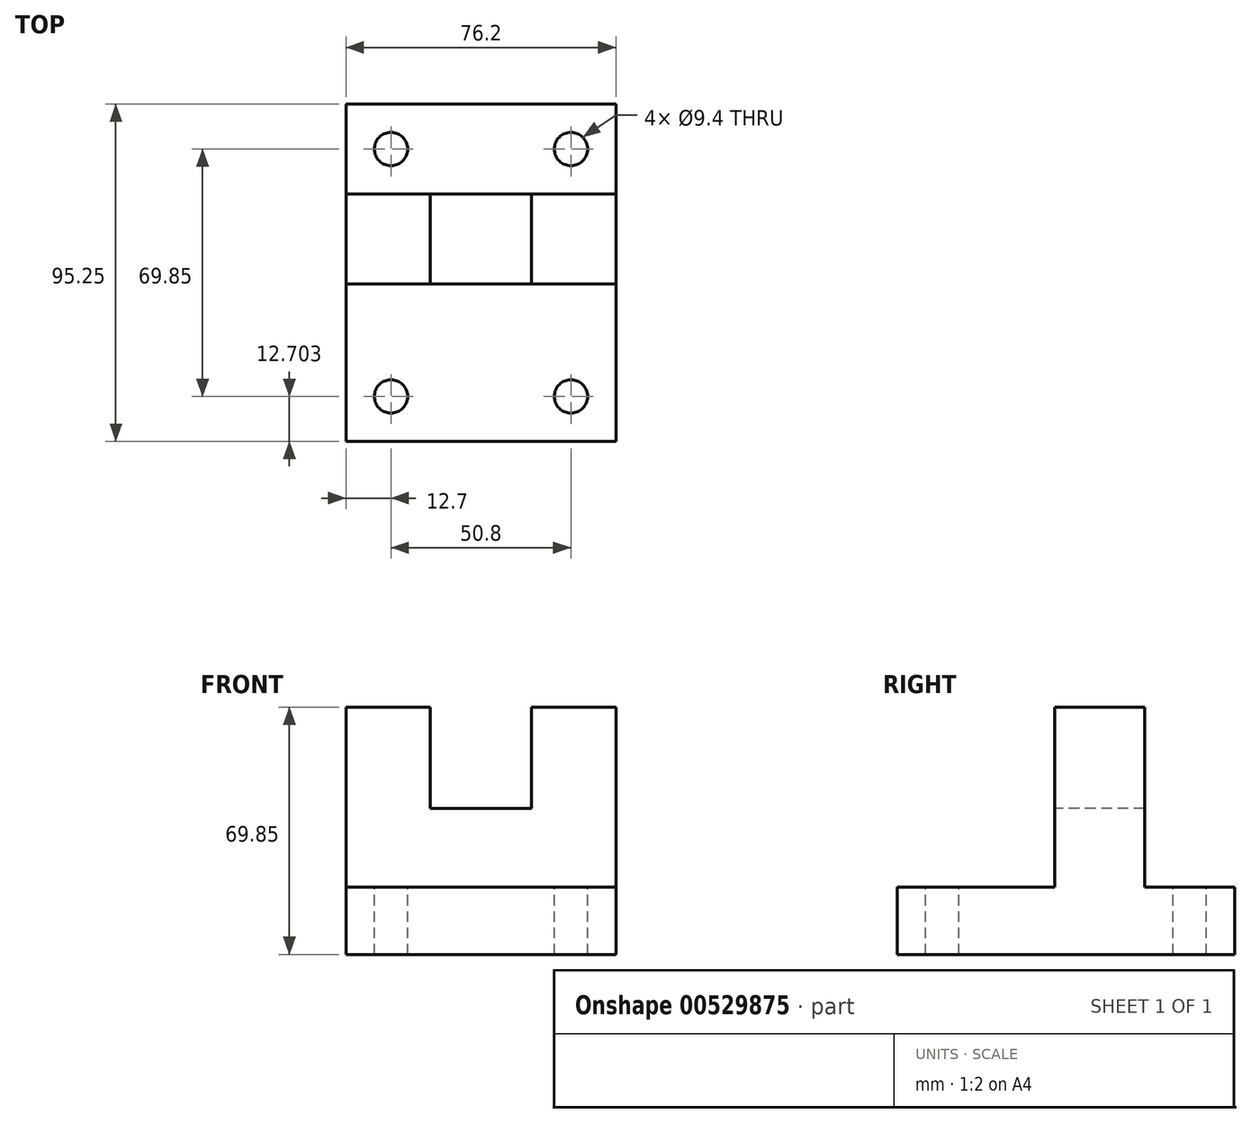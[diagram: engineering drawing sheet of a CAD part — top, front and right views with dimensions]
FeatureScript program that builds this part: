
annotation { "Feature Type Name" : "Feature", "Feature Type Description" : "" }
export const myFeature = defineFeature(function(context is Context, id is Id, definition is map)
    precondition{}
    {
        {
            var Q0;
            Q0=qCreatedBy(makeId("Right.planeOp"),FACE);
            var sketch = newSketch(context, id + "F0", { "sketchPlane" : qUnion([Q0])});
            skLineSegment(sketch, "E0", {"start": v(-57.19, -19.05) * mm, "end": v(38.06, -19.05) * mm});
            skLineSegment(sketch, "E1", {"start": v(38.06, -19.05) * mm, "end": v(38.06, 0) * mm});
            skLineSegment(sketch, "E2", {"start": v(-57.19, -19.05) * mm, "end": v(-57.19, 0) * mm});
            skLineSegment(sketch, "E3", {"start": v(-57.19, 0) * mm, "end": v(-12.74, 0) * mm});
            skLineSegment(sketch, "E4", {"start": v(-12.74, 0) * mm, "end": v(-12.74, 50.8) * mm});
            skLineSegment(sketch, "E5", {"start": v(-12.74, 50.8) * mm, "end": v(12.66, 50.8) * mm});
            skLineSegment(sketch, "E6", {"start": v(12.66, 50.8) * mm, "end": v(12.66, 0) * mm});
            skLineSegment(sketch, "E7", {"start": v(38.06, 0) * mm, "end": v(12.66, 0) * mm});
            skSolve(sketch);
        }
        {
            var Q0;
            Q0 = qSketchRegion(id + "F0", true);
            extrude(context, id + "F1", {"entities" : qUnion([Q0]), "depth" : 76.2 * mm, "offsetDistance" : 25.4 * mm});
        }
        {
            var Q0;
            Q0=qCreatedBy(makeId("Front.planeOp"),FACE);
            var sketch = newSketch(context, id + "F2", { "sketchPlane" : qUnion([Q0])});
            skPoint(sketch, "E8.0", {"position": v(38.1, 50.8) * mm});
            skLineSegment(sketch, "E9.bottom", {"start": v(23.81, 22.23) * mm, "end": v(52.39, 22.23) * mm});
            skLineSegment(sketch, "E9.top", {"start": v(23.81, 79.38) * mm, "end": v(52.39, 79.38) * mm});
            skLineSegment(sketch, "E9.left", {"start": v(23.81, 22.23) * mm, "end": v(23.81, 79.38) * mm});
            skLineSegment(sketch, "E9.right", {"start": v(52.39, 22.23) * mm, "end": v(52.39, 79.38) * mm});
            skSolve(sketch);
        }
        {
            var Q0;
            Q0=makeQuery(id+"F2.imprint","IMPRINT",FACE,{"disambiguationData":[TD([[makeQuery(id+"F2.imprint","IMPRINT",EDGE,{"derivedFrom":sQuery(id+"F2.wireOp",EDGE,"E9.bottom")}),1.0]])]});
            extrude(context, id + "F3", {"entities" : qUnion([Q0]), "operationType" : NewBodyOperationType.REMOVE, "endBound" : BoundingType.THROUGH_ALL, "oppositeDirection" : true, "depth" : 25.4 * mm, "offsetDistance" : 25.4 * mm, "hasSecondDirection" : true, "secondDirectionOppositeDirection" : false, "secondDirectionDepth" : 25.4 * mm});
        }
        {
            var Q0;
            Q0=qCreatedBy(makeId("Top.planeOp"),FACE);
            var sketch = newSketch(context, id + "F4", { "sketchPlane" : qUnion([Q0])});
            skCircle(sketch, "E10", {"center": v(63.5, -44.49) * mm, "radius": 4.7 * mm});
            skCircle(sketch, "E11", {"center": v(12.7, -44.49) * mm, "radius": 4.7 * mm});
            skCircle(sketch, "E12", {"center": v(12.7, 25.36) * mm, "radius": 4.7 * mm});
            skCircle(sketch, "E13", {"center": v(63.5, 25.36) * mm, "radius": 4.7 * mm});
            skSolve(sketch);
        }
        {
            var Q0;
            Q0=makeQuery(id+"F4.imprint","IMPRINT",FACE,{"disambiguationData":[TD([[makeQuery(id+"F4.imprint","IMPRINT",EDGE,{"derivedFrom":sQuery(id+"F4.wireOp",EDGE,"E12")}),1.0]])]});
            var Q1;
            Q1=makeQuery(id+"F4.imprint","IMPRINT",FACE,{"disambiguationData":[TD([[makeQuery(id+"F4.imprint","IMPRINT",EDGE,{"derivedFrom":sQuery(id+"F4.wireOp",EDGE,"E13")}),1.0]])]});
            var Q2;
            Q2=makeQuery(id+"F4.imprint","IMPRINT",FACE,{"disambiguationData":[TD([[makeQuery(id+"F4.imprint","IMPRINT",EDGE,{"derivedFrom":sQuery(id+"F4.wireOp",EDGE,"E11")}),1.0]])]});
            var Q3;
            Q3=makeQuery(id+"F4.imprint","IMPRINT",FACE,{"disambiguationData":[TD([[makeQuery(id+"F4.imprint","IMPRINT",EDGE,{"derivedFrom":sQuery(id+"F4.wireOp",EDGE,"E10")}),1.0]])]});
            extrude(context, id + "F5", {"entities" : qUnion([Q0, Q1, Q2, Q3]), "operationType" : NewBodyOperationType.REMOVE, "endBound" : BoundingType.THROUGH_ALL, "oppositeDirection" : true, "depth" : 25.4 * mm, "offsetDistance" : 25.4 * mm});
        }
    });
